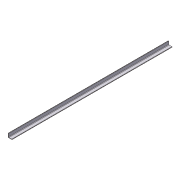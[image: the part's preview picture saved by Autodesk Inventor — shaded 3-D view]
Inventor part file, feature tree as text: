
AUTODESK INVENTOR PART (.ipt)
format: ipt  version: 2012 (Build 160160000, 160)  size: 77,312 bytes
history: native  units: in
note: dims shown in document units (in); Inventor stores cm internally (conversion verified against a paired STEP export)
features: extrude x1, sketch x1
ambient origin geometry x8: Origin, YZ Plane, XZ Plane, XY Plane, X Axis, Y Axis, Z Axis, Center Point
bodies: Solid1 (feature_tree)
feature tree (2):
  extrude  "Extrusion1"  Depth=84.0in TaperAngle=0.0deg
  sketch  "Sketch1"  dims[d0=2.0in d5=84.0in d6=0.0in d7=0.25in d14=0.25in d15=0.125in]
